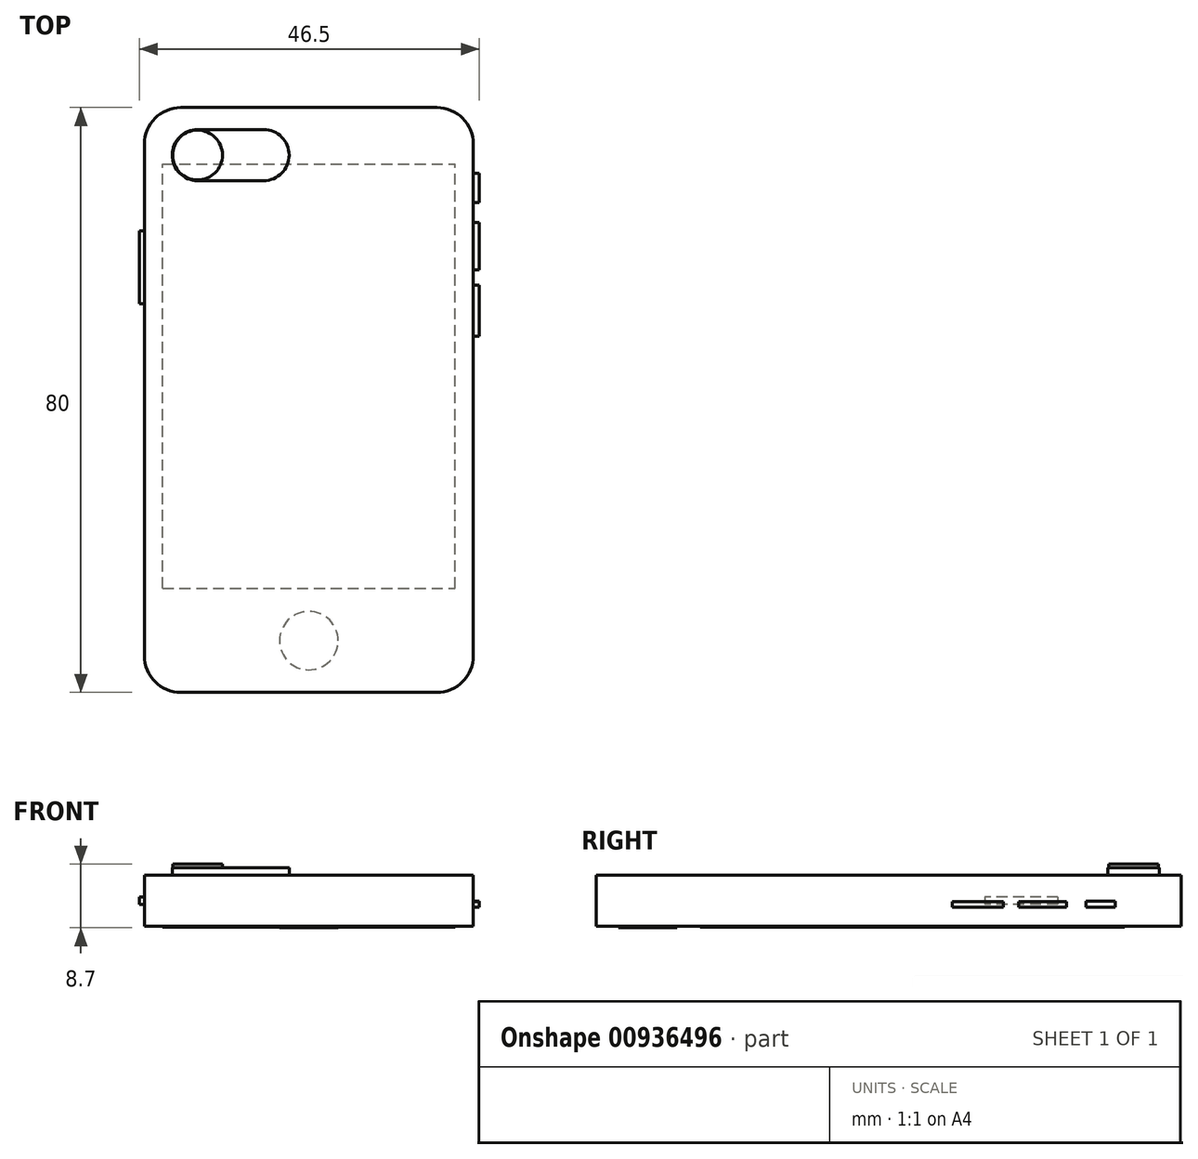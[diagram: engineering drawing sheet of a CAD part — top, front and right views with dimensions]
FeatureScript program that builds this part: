
annotation { "Feature Type Name" : "Feature", "Feature Type Description" : "" }
export const myFeature = defineFeature(function(context is Context, id is Id, definition is map)
    precondition{}
    {
        {
            var Q0;
            Q0=qCreatedBy(makeId("Top.planeOp"),FACE);
            var sketch = newSketch(context, id + "F0", { "sketchPlane" : qUnion([Q0])});
            skLineSegment(sketch, "E0.bottom", {"start": v(-19.8, 37.33) * mm, "end": v(25.2, 37.33) * mm});
            skLineSegment(sketch, "E0.top", {"start": v(-19.8, -42.67) * mm, "end": v(25.2, -42.67) * mm});
            skLineSegment(sketch, "E0.left", {"start": v(-19.8, 37.33) * mm, "end": v(-19.8, -42.67) * mm});
            skLineSegment(sketch, "E0.right", {"start": v(25.2, 37.33) * mm, "end": v(25.2, -42.67) * mm});
            skSolve(sketch);
        }
        {
            var Q0;
            Q0 = qSketchRegion(id + "F0", true);
            extrude(context, id + "F1", {"entities" : qUnion([Q0]), "depth" : 7 * mm, "offsetDistance" : 25 * mm});
        }
        {
            var Q0;
            Q0=makeQuery(id+"F1.opExtrude","SWEPT_EDGE",EDGE,{"disambiguationData":[OSD([sQuery(id+"F0.wireOp",EDGE,"E0.bottom"),sQuery(id+"F0.wireOp",EDGE,"E0.left")])]});
            var Q1;
            Q1=makeQuery(id+"F1.opExtrude","SWEPT_EDGE",EDGE,{"disambiguationData":[OSD([sQuery(id+"F0.wireOp",EDGE,"E0.bottom"),sQuery(id+"F0.wireOp",EDGE,"E0.right")])]});
            var Q2;
            Q2=makeQuery(id+"F1.opExtrude","SWEPT_EDGE",EDGE,{"disambiguationData":[OSD([sQuery(id+"F0.wireOp",EDGE,"E0.top"),sQuery(id+"F0.wireOp",EDGE,"E0.left")])]});
            var Q3;
            Q3=makeQuery(id+"F1.opExtrude","SWEPT_EDGE",EDGE,{"disambiguationData":[OSD([sQuery(id+"F0.wireOp",EDGE,"E0.top"),sQuery(id+"F0.wireOp",EDGE,"E0.right")])]});
            fillet(context, id + "F2", {"entities" : qUnion([Q0, Q1, Q2, Q3]), "radius" : 5 * mm, "tangentPropagation" : true, "allowEdgeOverflow" : false});
        }
        {
            var Q0;
            Q0=qCreatedBy(makeId("Top.planeOp"),FACE);
            var sketch = newSketch(context, id + "F3", { "sketchPlane" : qUnion([Q0])});
            skLineSegment(sketch, "E1.bottom", {"start": v(-12.5, 34.33) * mm, "end": v(-3.5, 34.33) * mm});
            skLineSegment(sketch, "E1.top", {"start": v(-12.5, 27.33) * mm, "end": v(-3.5, 27.33) * mm});
            skLineSegment(sketch, "E1.left", {"start": v(-16, 30.83) * mm, "end": v(-16, 30.83) * mm});
            skLineSegment(sketch, "E1.right", {"start": v(0, 30.83) * mm, "end": v(0, 30.83) * mm});
            skPoint(sketch, "E2.visualSharp", {"position": v(-16, 34.33) * mm});
            skArc(sketch, "E2.filletArc", {"start": v(-12.5, 34.33) * mm, "mid": v(-14.97, 33.3) * mm, "end": v(-16, 30.83) * mm});
            skPoint(sketch, "E3.visualSharp", {"position": v(-16, 27.33) * mm});
            skArc(sketch, "E3.filletArc", {"start": v(-16, 30.83) * mm, "mid": v(-14.97, 28.36) * mm, "end": v(-12.5, 27.33) * mm});
            skPoint(sketch, "E4.visualSharp", {"position": v(0, 27.33) * mm});
            skArc(sketch, "E4.filletArc", {"start": v(-3.5, 27.33) * mm, "mid": v(-1.03, 28.36) * mm, "end": v(0, 30.83) * mm});
            skPoint(sketch, "E5.visualSharp", {"position": v(0, 34.33) * mm});
            skArc(sketch, "E5.filletArc", {"start": v(0, 30.83) * mm, "mid": v(-1.03, 33.3) * mm, "end": v(-3.5, 34.33) * mm});
            skSolve(sketch);
        }
        {
            var Q0;
            Q0 = qSketchRegion(id + "F3", true);
            extrude(context, id + "F4", {"entities" : qUnion([Q0]), "operationType" : NewBodyOperationType.ADD, "depth" : 8 * mm, "offsetDistance" : 25 * mm});
        }
        {
            var Q0;
            Q0=qCreatedBy(makeId("Top.planeOp"),FACE);
            var sketch = newSketch(context, id + "F5", { "sketchPlane" : qUnion([Q0])});
            skCircle(sketch, "E6", {"center": v(-12.53, 30.83) * mm, "radius": 3.4 * mm});
            skSolve(sketch);
        }
        {
            var Q0;
            Q0 = qSketchRegion(id + "F5", true);
            extrude(context, id + "F6", {"entities" : qUnion([Q0]), "operationType" : NewBodyOperationType.ADD, "depth" : 8.5 * mm, "offsetDistance" : 25 * mm});
        }
        {
            var Q0;
            Q0=qCreatedBy(makeId("Right.planeOp"),FACE);
            var sketch = newSketch(context, id + "F7", { "sketchPlane" : qUnion([Q0])});
            skLineSegment(sketch, "E7.bottom", {"start": v(24.33, 3.42) * mm, "end": v(28.33, 3.42) * mm});
            skLineSegment(sketch, "E7.top", {"start": v(24.33, 2.62) * mm, "end": v(28.33, 2.62) * mm});
            skLineSegment(sketch, "E7.left", {"start": v(24.33, 3.42) * mm, "end": v(24.33, 2.62) * mm});
            skLineSegment(sketch, "E7.right", {"start": v(28.33, 3.42) * mm, "end": v(28.33, 2.62) * mm});
            skSolve(sketch);
        }
        {
            var Q0;
            Q0 = qSketchRegion(id + "F7", true);
            extrude(context, id + "F8", {"entities" : qUnion([Q0]), "operationType" : NewBodyOperationType.ADD, "depth" : 26 * mm, "offsetDistance" : 25 * mm});
        }
        {
            var Q0;
            Q0=qCreatedBy(makeId("Right.planeOp"),FACE);
            var sketch = newSketch(context, id + "F9", { "sketchPlane" : qUnion([Q0])});
            skLineSegment(sketch, "E8.bottom", {"start": v(15.14, 3.4) * mm, "end": v(21.64, 3.4) * mm});
            skLineSegment(sketch, "E8.top", {"start": v(15.14, 2.6) * mm, "end": v(21.64, 2.6) * mm});
            skLineSegment(sketch, "E8.left", {"start": v(15.14, 3.4) * mm, "end": v(15.14, 2.6) * mm});
            skLineSegment(sketch, "E8.right", {"start": v(21.64, 3.4) * mm, "end": v(21.64, 2.6) * mm});
            skSolve(sketch);
        }
        {
            var Q0;
            Q0 = qSketchRegion(id + "F9", true);
            extrude(context, id + "F10", {"entities" : qUnion([Q0]), "operationType" : NewBodyOperationType.ADD, "depth" : 26 * mm, "offsetDistance" : 25 * mm});
        }
        {
            var Q0;
            Q0=qCreatedBy(makeId("Right.planeOp"),FACE);
            var sketch = newSketch(context, id + "F11", { "sketchPlane" : qUnion([Q0])});
            skLineSegment(sketch, "E9.bottom", {"start": v(6.04, 3.4) * mm, "end": v(13.04, 3.4) * mm});
            skLineSegment(sketch, "E9.top", {"start": v(6.04, 2.6) * mm, "end": v(13.04, 2.6) * mm});
            skLineSegment(sketch, "E9.left", {"start": v(6.04, 3.4) * mm, "end": v(6.04, 2.6) * mm});
            skLineSegment(sketch, "E9.right", {"start": v(13.04, 3.4) * mm, "end": v(13.04, 2.6) * mm});
            skSolve(sketch);
        }
        {
            var Q0;
            Q0 = qSketchRegion(id + "F11", true);
            extrude(context, id + "F12", {"entities" : qUnion([Q0]), "operationType" : NewBodyOperationType.ADD, "depth" : 26 * mm, "offsetDistance" : 25 * mm});
        }
        {
            var Q0;
            Q0=qCreatedBy(makeId("Right.planeOp"),FACE);
            var sketch = newSketch(context, id + "F13", { "sketchPlane" : qUnion([Q0])});
            skLineSegment(sketch, "E10.bottom", {"start": v(20.47, 4) * mm, "end": v(10.47, 4) * mm});
            skLineSegment(sketch, "E10.top", {"start": v(20.47, 3) * mm, "end": v(10.47, 3) * mm});
            skLineSegment(sketch, "E10.left", {"start": v(20.47, 4) * mm, "end": v(20.47, 3) * mm});
            skLineSegment(sketch, "E10.right", {"start": v(10.47, 4) * mm, "end": v(10.47, 3) * mm});
            skSolve(sketch);
        }
        {
            var Q0;
            Q0 = qSketchRegion(id + "F13", true);
            extrude(context, id + "F14", {"entities" : qUnion([Q0]), "operationType" : NewBodyOperationType.ADD, "depth" : -20.5 * mm, "offsetDistance" : 25 * mm});
        }
        {
            var Q0;
            Q0=qCreatedBy(makeId("Top.planeOp"),FACE);
            var sketch = newSketch(context, id + "F15", { "sketchPlane" : qUnion([Q0])});
            skCircle(sketch, "E11", {"center": v(2.7, -35.6) * mm, "radius": 4 * mm});
            skSolve(sketch);
        }
        {
            var Q0;
            Q0 = qSketchRegion(id + "F15", true);
            extrude(context, id + "F16", {"entities" : qUnion([Q0]), "operationType" : NewBodyOperationType.ADD, "depth" : -0.2 * mm, "offsetDistance" : 25 * mm});
        }
        {
            var Q0;
            Q0=qCreatedBy(makeId("Top.planeOp"),FACE);
            var sketch = newSketch(context, id + "F17", { "sketchPlane" : qUnion([Q0])});
            skLineSegment(sketch, "E12.bottom", {"start": v(-17.3, -28.42) * mm, "end": v(22.7, -28.42) * mm});
            skLineSegment(sketch, "E12.top", {"start": v(-17.3, 29.58) * mm, "end": v(22.7, 29.58) * mm});
            skLineSegment(sketch, "E12.left", {"start": v(-17.3, -28.42) * mm, "end": v(-17.3, 29.58) * mm});
            skLineSegment(sketch, "E12.right", {"start": v(22.7, -28.42) * mm, "end": v(22.7, 29.58) * mm});
            skSolve(sketch);
        }
        {
            var Q0;
            Q0 = qSketchRegion(id + "F17", true);
            extrude(context, id + "F18", {"entities" : qUnion([Q0]), "operationType" : NewBodyOperationType.ADD, "depth" : -0.1 * mm, "offsetDistance" : 25 * mm});
        }
    });
